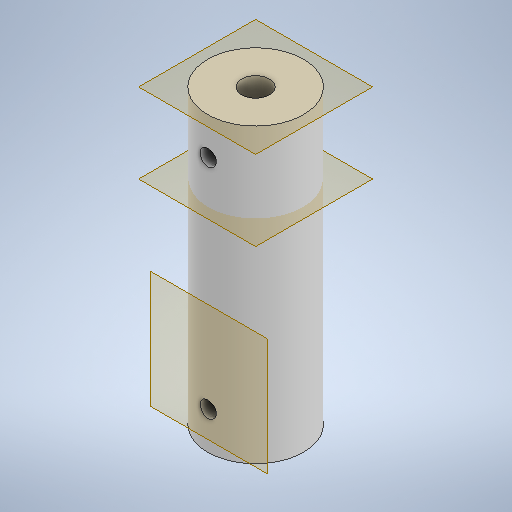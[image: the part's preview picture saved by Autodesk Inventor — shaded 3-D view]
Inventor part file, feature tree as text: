
AUTODESK INVENTOR PART (.ipt)
format: ipt  version: 2025.1 (Build 291241000, 241)  size: 591,360 bytes
history: native  units: mm
features: other x6, sketch x6, hole x4, extrude x2
ambient origin geometry x8: Origin, YZ Plane, XZ Plane, XY Plane, X Axis, Y Axis, Z Axis, Center Point
bodies: Body1 (feature_tree)
feature tree (18):
  other  "ソリッド1"
  extrude  "押し出し1"  Depth=18.0mm
  hole  "穴1"  [1 undecoded]
  other  "作業平面1"
  hole  "穴2"  [1 undecoded]
  other  "作業平面4"
  extrude  "押し出し2"  TaperAngle=0.0deg  [1 undecoded]
  other  "作業平面5"
  hole  "穴3"  [1 undecoded]
  hole  "穴4"  [1 undecoded]
  other  "作業平面7"
  other  "作業平面8"
  sketch  "スケッチ1"
  sketch  "スケッチ2"
  sketch  "スケッチ3"
  sketch  "スケッチ5"
  sketch  "スケッチ6"
  sketch  "スケッチ7"
note: 5 required parameter values undecoded (feature->parameter linkage not recoverable at this tier; creation-order binding heuristic only, values carry confidence <= 0.55)
